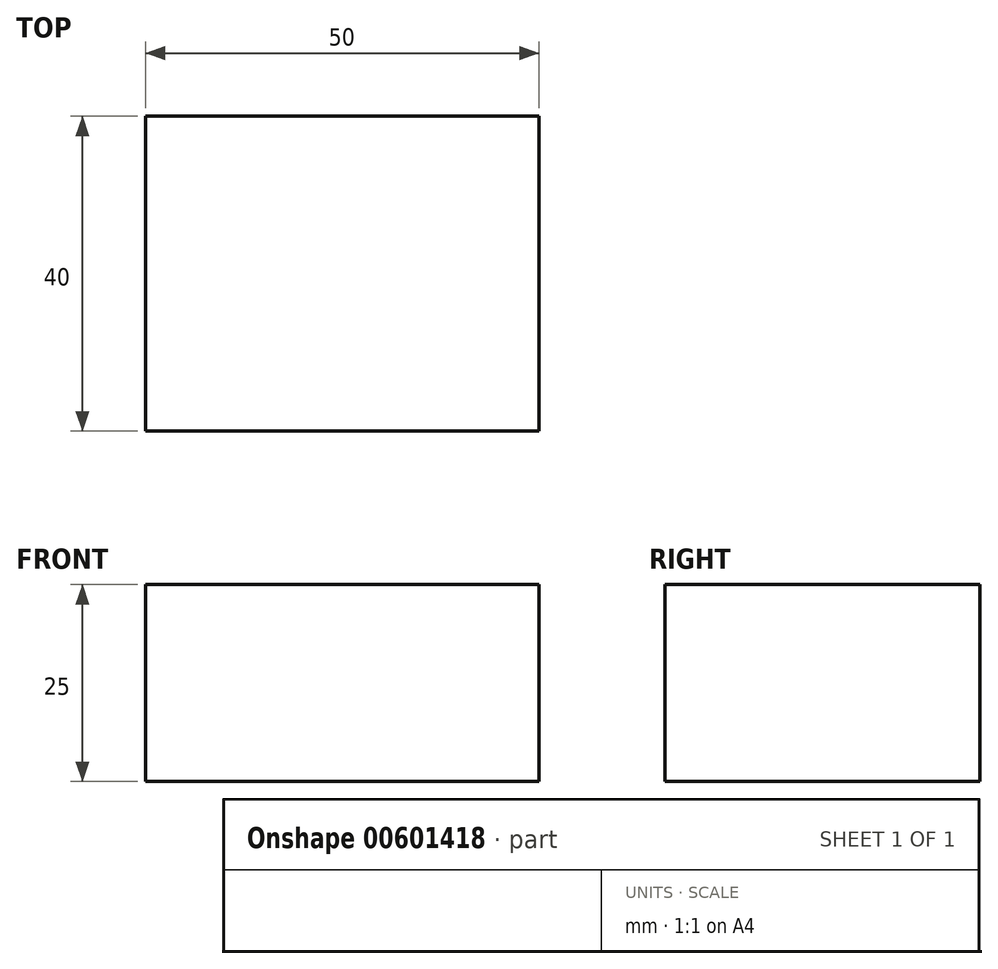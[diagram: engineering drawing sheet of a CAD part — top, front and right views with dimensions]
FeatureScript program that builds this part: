
annotation { "Feature Type Name" : "Feature", "Feature Type Description" : "" }
export const myFeature = defineFeature(function(context is Context, id is Id, definition is map)
    precondition{}
    {
        {
            var Q0;
            Q0=qCreatedBy(makeId("Top.planeOp"),FACE);
            var sketch = newSketch(context, id + "F0", { "sketchPlane" : qUnion([Q0])});
            skLineSegment(sketch, "E0.bottom", {"start": v(0, 0) * mm, "end": v(50, 0) * mm});
            skLineSegment(sketch, "E0.top", {"start": v(0, 40) * mm, "end": v(50, 40) * mm});
            skLineSegment(sketch, "E0.left", {"start": v(0, 0) * mm, "end": v(0, 40) * mm});
            skLineSegment(sketch, "E0.right", {"start": v(50, 0) * mm, "end": v(50, 40) * mm});
            skSolve(sketch);
        }
        {
            var Q0;
            Q0=makeQuery(id+"F0.imprint","IMPRINT",FACE,{"disambiguationData":[TD([[makeQuery(id+"F0.imprint","IMPRINT",EDGE,{"derivedFrom":sQuery(id+"F0.wireOp",EDGE,"E0.bottom")}),1.0]])]});
            extrude(context, id + "F1", {"entities" : qUnion([Q0]), "depth" : 25 * mm, "offsetDistance" : 25 * mm});
        }
    });
